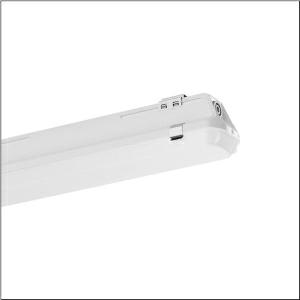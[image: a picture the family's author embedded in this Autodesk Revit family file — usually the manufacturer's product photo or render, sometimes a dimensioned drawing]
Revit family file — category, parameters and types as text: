
# Revit family: monsun_r__11_51fp20ep460h_939a
name_source: partatom
category: Lighting Fixtures
units: mm (PartAtom-declared; Revit-internal decimal feet)

## family parameters
Cut with Voids When Loaded = No
Host = Face
Light Source = No
Part Type = Normal
Room Calculation Point = No
Round Connector Dimension = Use Diameter
Shared = No

## types (1)
- --- (1 x LED, 5450 lm, 34.6 W, 4000K)
    Apparent Load = 35 VA
    CIE Flux Codes = 45 75 93 94 100
    Color Rendering = 80
    Color Temperature = 4000K
    Default Elevation = 1800 mm
    Description = Monsun® 11, damp-proof luminaire, chain hanger, primary optical cover: enclosure, of PC, light emission: direct distribution, primary light characteristic: symmetric, installation type: suspended mounting, surface-mounted, horizontal mounting, vertical mounting, LED, rated luminous flux: 5.450lm, luminous efficacy: 158lm/W, light colour: 840, colour temperature: 4000K, control gear: ECG DALI, with terminal, 5-pole, max. 2.5mm², mains connection: 220..240V, AC, 50/60Hz, rated input power: 35W, luminaire housing, of glass-fibre reinforced polyester, uncoated, bright grey, incl. chain hanger, length: 1.590mm, width: 90mm, height: 88mm, clip for enclosure, of stainless steel (V2A), ceiling mounting element, of stainless steel (V2A), chain hanger, of stainless steel (V2A), protection rating (complete): IP66, insulation class (complete): insulation class I (protective earthing), certification: CE, ENEC, VDE, UKCA, protection symbol: D, impact resistance: IK08, permissible operating ambient temperature: -25..+40°C, standard: EN 50419, EN 60598-2-1, no direct snow, no direct sun, no direct rain, for indoor or canopied outdoor use, corresponds to IFS (International Featured Standards) requirements for safety and quality in the food industry, contact your sales advisor before using the luminaires in applications with unclear chemical exposure, large temperature fluctuations or condensation-forming humidity, LABS conformity tested according to VDMA 24364:2018-05, packaging unit: 1 piece
    Height = 89 mm
    Lamp = 1 x LED
    Lamp Light Flux = 5450 lm
    Lamp Power = 34.6 W
    Lamp count = 1
    Length = 1590 mm
    Luminous efficacy = 158 lm/W
    Manufacturer = Siteco
    ModVariant = No
    Model = 51FP20EP460H
    Mounting Place = Ceiling
    Mounting Type = Surface mounted
    Number of Poles = 1
    OnlyDefault = Yes
    Power Factor = 1
    Product Name = Monsun® 11
    Product group = damp-proof luminaire
    ProductGroupID = 301
    Protection Class = Protection class I
    Protection Degree = IP 66
    RLX_Detail_Level = 1
    RLX_Emergency_Light_Flux = 0 lm
    RLX_Emergency_Type = 0
    RLX_Emergency_Type_DB = No
    RlxData = <blob elided: 92365 chars, md5=c3475303>
    Socket = socket
    Standby Power = 0 W
    System Light Flux = 5450 lm
    System Power = 35 W
    Type Comments = factory setting: luminous flux: 100 % | dim-lin: 254 | 232 mA
    Type Image = l_1004748.jpg
    URL = http://relux.com
    VarID = @adj_156447
    Voltage = 0 V
    Weight = 0.00 kg
    Width = 90 mm

## geometry (parser evidence)
native form markers: Blend x4, Sweep x15
no freeform markers — native parametric forms only
